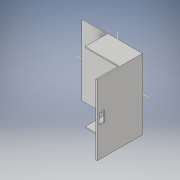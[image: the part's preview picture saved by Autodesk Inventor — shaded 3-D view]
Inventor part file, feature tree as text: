
AUTODESK INVENTOR PART (.ipt)
format: ipt  version: 2019.4 (Build 234330000, 330)  size: 150,528 bytes
history: native  units: mm
features: extrude x5, sketch x5, plane x1, mirror x1
ambient origin geometry x8: Origin, YZ Plane, XZ Plane, XY Plane, X Axis, Y Axis, Z Axis, Center Point
bodies: Body1 (feature_tree)
feature tree (12):
  extrude  "Extrusion2"  Depth=1.0mm TaperAngle=0.0deg
  extrude  "Extrusion3"  Depth=1.0mm TaperAngle=0.0deg
  extrude  "Extrusion4"  Depth=65.0mm
  plane  "Work Plane2"
  mirror  "Mirror3"
  extrude  "Extrusion5"  Depth=21.0mm TaperAngle=0.0deg
  extrude  "Extrusion6"  Depth=5.0mm
  sketch  "Sketch2"  dims[d5=1.0mm d6=0.0mm d7=1.0mm d8=0.0mm]
  sketch  "Sketch3"  dims[d9=20.0mm d11=1.0mm d12=0.0mm]
  sketch  "Sketch4"  dims[d13=54.0mm d14=65.0mm]
  sketch  "Sketch5"  dims[d15=32.0mm d16=21.0mm d17=0.0mm]
  sketch  "Sketch6"  dims[d18=2.0mm d19=5.0mm d20=10.0mm d21=21.0mm d22=0.0mm]
